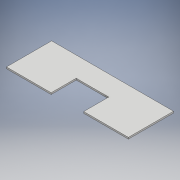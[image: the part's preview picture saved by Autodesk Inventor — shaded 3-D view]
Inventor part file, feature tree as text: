
AUTODESK INVENTOR PART (.ipt)
format: ipt  version: 2018 (Build 220112000, 112)  size: 100,864 bytes
history: native  units: mm
features: extrude x1, sketch x1
ambient origin geometry x8: Origin, YZ Plane, XZ Plane, XY Plane, X Axis, Y Axis, Z Axis, Center Point
bodies: Solid1 (feature_tree)
feature tree (2):
  extrude  "Extrusion1"  Depth=45.0mm
  sketch  "Sketch1"  dims[d11=44.5mm d12=45.0mm d13=32.5mm d14=20.0mm d15=44.5mm d16=45.0mm d17=1.6mm d18=0.0mm]
